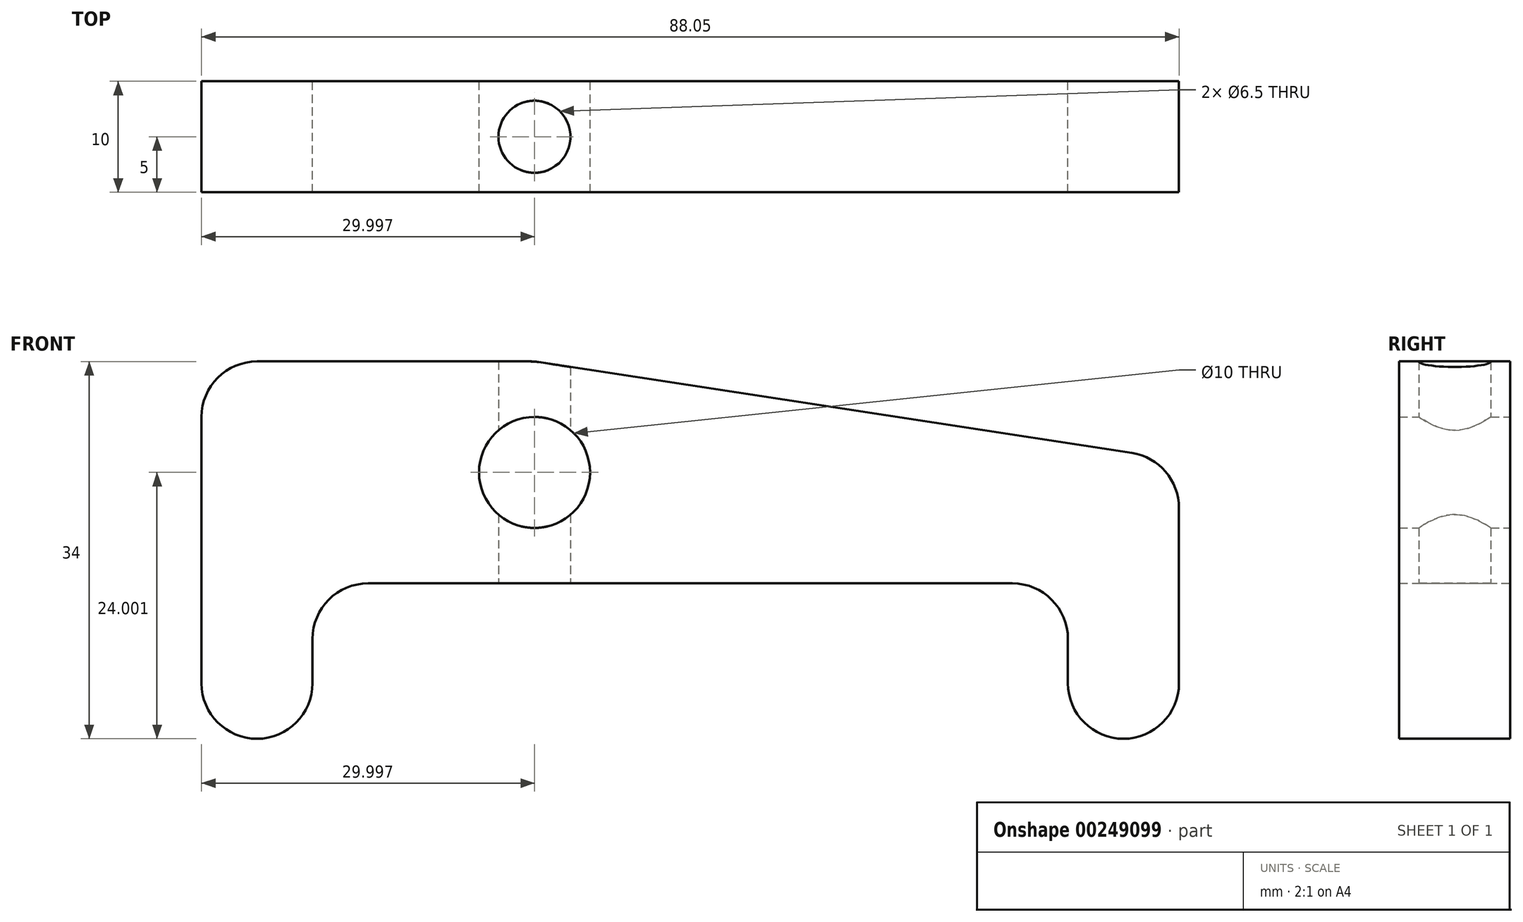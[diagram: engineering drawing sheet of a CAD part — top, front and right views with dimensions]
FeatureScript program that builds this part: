
annotation { "Feature Type Name" : "Feature", "Feature Type Description" : "" }
export const myFeature = defineFeature(function(context is Context, id is Id, definition is map)
    precondition{}
    {
        {
            var Q0;
            Q0=qCreatedBy(makeId("Front.planeOp"),FACE);
            var sketch = newSketch(context, id + "F0", { "sketchPlane" : qUnion([Q0])});
            skCircle(sketch, "E0", {"center": v(-43.68, 33.21) * mm, "radius": 5 * mm});
            skLineSegment(sketch, "E1", {"start": v(-68.68, 9.21) * mm, "end": v(-68.68, 9.21) * mm});
            skLineSegment(sketch, "E2", {"start": v(-63.68, 14.21) * mm, "end": v(-63.68, 18.21) * mm});
            skLineSegment(sketch, "E3", {"start": v(-58.68, 23.21) * mm, "end": v(-0.63, 23.21) * mm});
            skLineSegment(sketch, "E4", {"start": v(4.37, 18.21) * mm, "end": v(4.37, 14.21) * mm});
            skLineSegment(sketch, "E5", {"start": v(9.37, 9.21) * mm, "end": v(9.37, 9.21) * mm});
            skLineSegment(sketch, "E6", {"start": v(14.37, 14.21) * mm, "end": v(14.37, 30.02) * mm});
            skLineSegment(sketch, "E7", {"start": v(-44.06, 43.21) * mm, "end": v(-68.68, 43.21) * mm});
            skLineSegment(sketch, "E8", {"start": v(-73.68, 38.21) * mm, "end": v(-73.68, 14.21) * mm});
            skLineSegment(sketch, "E9", {"start": v(10.13, 34.96) * mm, "end": v(-43.3, 43.15) * mm});
            skPoint(sketch, "E10.visualSharp", {"position": v(-73.68, 43.21) * mm});
            skArc(sketch, "E10.filletArc", {"start": v(-68.68, 43.21) * mm, "mid": v(-72.22, 41.75) * mm, "end": v(-73.68, 38.21) * mm});
            skPoint(sketch, "E11.visualSharp", {"position": v(-43.68, 43.21) * mm});
            skArc(sketch, "E11.filletArc", {"start": v(-43.3, 43.15) * mm, "mid": v(-43.68, 43.2) * mm, "end": v(-44.06, 43.21) * mm});
            skPoint(sketch, "E12.visualSharp", {"position": v(14.37, 34.3) * mm});
            skArc(sketch, "E12.filletArc", {"start": v(14.37, 30.02) * mm, "mid": v(13.16, 33.27) * mm, "end": v(10.13, 34.96) * mm});
            skPoint(sketch, "E13.visualSharp", {"position": v(14.37, 9.21) * mm});
            skArc(sketch, "E13.filletArc", {"start": v(9.37, 9.21) * mm, "mid": v(12.9, 10.67) * mm, "end": v(14.37, 14.21) * mm});
            skPoint(sketch, "E14.visualSharp", {"position": v(4.37, 9.21) * mm});
            skArc(sketch, "E14.filletArc", {"start": v(4.37, 14.21) * mm, "mid": v(5.83, 10.67) * mm, "end": v(9.37, 9.21) * mm});
            skPoint(sketch, "E15.visualSharp", {"position": v(4.37, 23.21) * mm});
            skArc(sketch, "E15.filletArc", {"start": v(4.37, 18.21) * mm, "mid": v(2.9, 21.75) * mm, "end": v(-0.63, 23.21) * mm});
            skPoint(sketch, "E16.visualSharp", {"position": v(-63.68, 23.21) * mm});
            skArc(sketch, "E16.filletArc", {"start": v(-58.68, 23.21) * mm, "mid": v(-62.22, 21.75) * mm, "end": v(-63.68, 18.21) * mm});
            skPoint(sketch, "E17.visualSharp", {"position": v(-63.68, 9.21) * mm});
            skArc(sketch, "E17.filletArc", {"start": v(-68.68, 9.21) * mm, "mid": v(-65.15, 10.67) * mm, "end": v(-63.68, 14.21) * mm});
            skPoint(sketch, "E18.visualSharp", {"position": v(-73.68, 9.21) * mm});
            skArc(sketch, "E18.filletArc", {"start": v(-73.68, 14.21) * mm, "mid": v(-72.22, 10.67) * mm, "end": v(-68.68, 9.21) * mm});
            skSolve(sketch);
        }
        {
            var Q0;
            Q0 = qSketchRegion(id + "F0", true);
            extrude(context, id + "F1", {"entities" : qUnion([Q0]), "depth" : 10 * mm});
        }
        {
            var Q0;
            Q0=makeQuery(id+"F1.opExtrude","SWEPT_FACE",FACE,{"disambiguationData":[OSD([sQuery(id+"F0.wireOp",EDGE,"E3")])]});
            var sketch = newSketch(context, id + "F2", { "sketchPlane" : qUnion([Q0])});
            skCircle(sketch, "E19", {"center": v(-43.68, 5) * mm, "radius": 3.25 * mm});
            skSolve(sketch);
        }
        {
            var Q0;
            Q0 = qSketchRegion(id + "F2", true);
            extrude(context, id + "F3", {"entities" : qUnion([Q0]), "operationType" : NewBodyOperationType.REMOVE, "endBound" : BoundingType.THROUGH_ALL, "oppositeDirection" : true, "depth" : 25 * mm});
        }
    });
